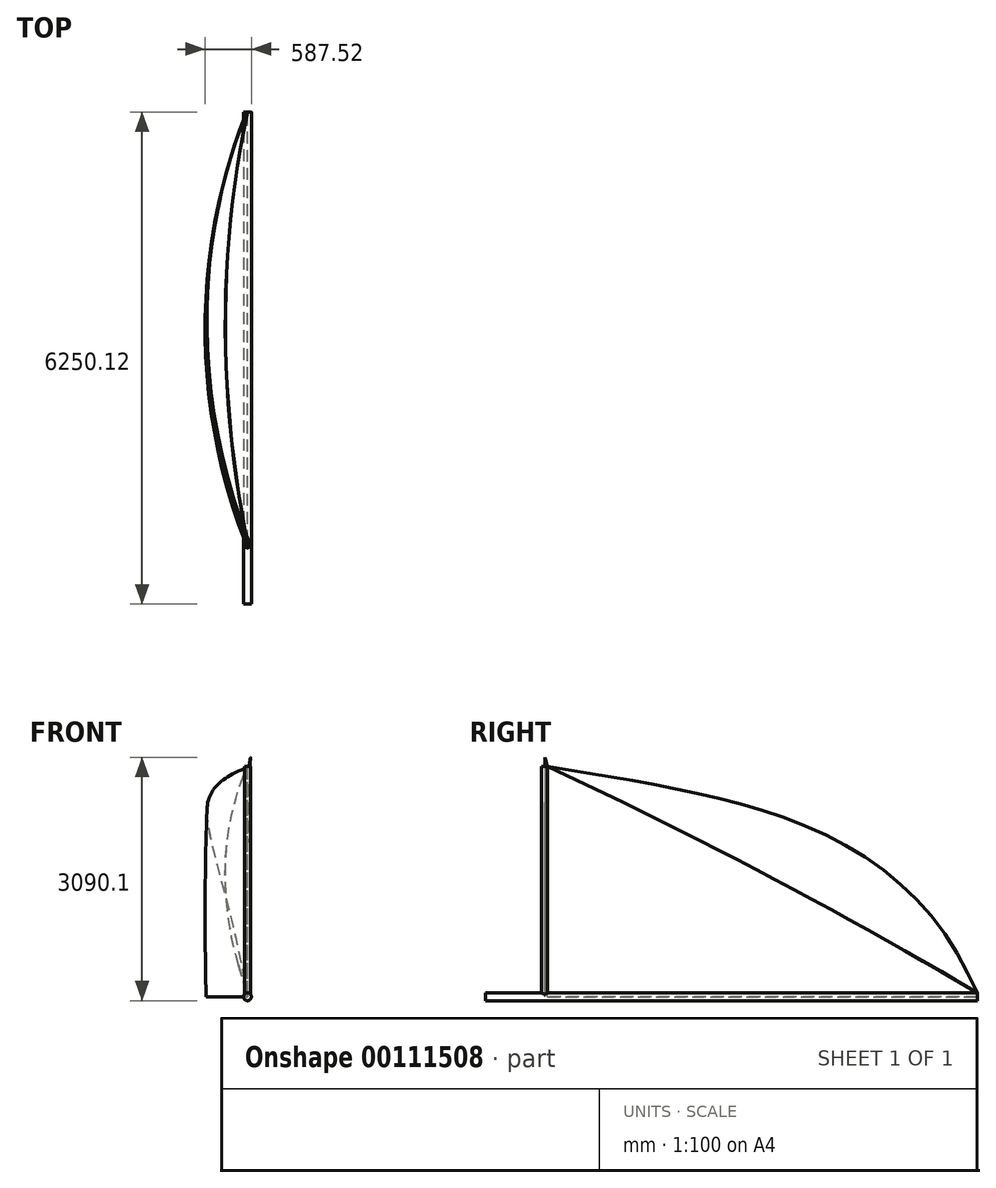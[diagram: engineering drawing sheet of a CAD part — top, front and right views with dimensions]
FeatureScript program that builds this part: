
annotation { "Feature Type Name" : "Feature", "Feature Type Description" : "" }
export const myFeature = defineFeature(function(context is Context, id is Id, definition is map)
    precondition{}
    {
        {
            var Q0;
            Q0=qCreatedBy(makeId("Front.planeOp"),FACE);
            var sketch = newSketch(context, id + "F0", { "sketchPlane" : qUnion([Q0])});
            skCircle(sketch, "E0", {"center": v(0, 0) * mm, "radius": 50 * mm});
            skSolve(sketch);
        }
        {
            var Q0;
            Q0=qSketchRegion(id+"F0",true);
            extrude(context, id + "F1", {"entities" : qUnion([Q0]), "oppositeDirection" : true, "depth" : 6250 * mm});
        }
        {
            var Q0;
            Q0=qCreatedBy(makeId("Top.planeOp"),FACE);
            var sketch = newSketch(context, id + "F2", { "sketchPlane" : qUnion([Q0])});
            skLineSegment(sketch, "E1", {"start": v(-50, 0) * mm, "end": v(-50, 6250) * mm});
            skLineSegment(sketch, "E2", {"start": v(50, 6250) * mm, "end": v(50, 0) * mm});
            skLineSegment(sketch, "E3", {"start": v(0, 750) * mm, "end": v(-50, 750) * mm});
            skLineSegment(sketch, "E4", {"start": v(0, 750) * mm, "end": v(50, 750) * mm});
            skCircle(sketch, "E5", {"center": v(0, 750) * mm, "radius": 37.5 * mm});
            skSolve(sketch);
        }
        {
            var Q0;
            Q0=qSketchRegion(id+"F2",true);
            extrude(context, id + "F3", {"entities" : qUnion([Q0]), "operationType" : NewBodyOperationType.ADD, "depth" : 2925 * mm});
        }
        {
            var Q0;
            Q0=qCreatedBy(makeId("Top.planeOp"),FACE);
            var sketch = newSketch(context, id + "F4", { "sketchPlane" : qUnion([Q0])});
            skPoint(sketch, "E6.0", {"position": v(0, 750) * mm});
            skLineSegment(sketch, "E7.0", {"start": v(50, 6250) * mm, "end": v(-50, 6250) * mm});
            skPoint(sketch, "E8", {"position": v(0, 6250) * mm});
            skArc(sketch, "E9", {"start": v(0, 6250) * mm, "mid": v(-524.4, 3500) * mm, "end": v(0, 750) * mm});
            skLineSegment(sketch, "E10", {"start": v(6948.32, -1070.1) * mm, "end": v(6948.32, 10785.69) * mm, "construction": true});
            skArc(sketch, "E11.0", {"start": v(-1.08, 6250) * mm, "mid": v(-525.4, 3500) * mm, "end": v(-1.08, 750) * mm});
            skLineSegment(sketch, "E12", {"start": v(0, 6250) * mm, "end": v(-1.08, 6250) * mm});
            skLineSegment(sketch, "E13", {"start": v(0, 750) * mm, "end": v(-1.08, 750) * mm});
            skSolve(sketch);
        }
        {
            var Q0;
            Q0=qSketchRegion(id+"F4",true);
            var Q1;
            Q1=sQuery(id+"F4.wireOp",EDGE,"E9");
            var Q2;
            Q2=sQuery(id+"F4.wireOp",EDGE,"E10");
            revolve(context, id + "F5", {"bodyType" : ToolBodyType.SURFACE, "entities" : qUnion([Q0]), "surfaceEntities" : qUnion([Q1]), "axis" : qUnion([Q2]), "revolveType" : RevolveType.FULL});
        }
        {
            var Q0;
            Q0=qCreatedBy(makeId("Top.planeOp"),FACE);
            cPlane(context, id + "F6", {"entities" : qUnion([Q0]), "cplaneType" : CPlaneType.OFFSET, "offset" : 1000 * mm, "width" : 150 * mm, "height" : 150 * mm});
        }
        {
            var Q0;
            Q0=qCreatedBy(id+"F6.planeOp",FACE);
            var sketch = newSketch(context, id + "F7", { "sketchPlane" : qUnion([Q0])});
            skLineSegment(sketch, "E14", {"start": v(41794.72, -2246.79) * mm, "end": v(45677.07, -23348.96) * mm, "construction": true});
            skSolve(sketch);
        }
        {
            var Q0;
            Q0=makeQuery(id+"F4.imprint","IMPRINT",FACE,{"disambiguationData":[TD([[makeQuery(id+"F4.imprint","IMPRINT",EDGE,{"derivedFrom":sQuery(id+"F4.wireOp",EDGE,"E9")}),-1.0]])]});
            var Q1;
            Q1=sQuery(id+"F4.wireOp",EDGE,"E9");
            var Q2;
            Q2=sQuery(id+"F7.wireOp",EDGE,"E14");
            revolve(context, id + "F8", {"entities" : qUnion([Q0]), "surfaceEntities" : qUnion([Q1]), "axis" : qUnion([Q2]), "revolveType" : RevolveType.ONE_DIRECTION, "oppositeDirection" : true, "angle" : 12 * degree});
        }
        {
            var Q0;
            Q0=qCreatedBy(makeId("Right.planeOp"),FACE);
            var sketch = newSketch(context, id + "F9", { "sketchPlane" : qUnion([Q0])});
            skLineSegment(sketch, "E15.0", {"start": v(712.5, 2925) * mm, "end": v(787.5, 2925) * mm});
            skLineSegment(sketch, "E16.0", {"start": v(6250, -50) * mm, "end": v(6250, 50) * mm});
            skFitSpline(sketch, "E17", {"points": [v(6250, 50) * mm, v(5690.7, 991.83) * mm, v(4190.9, 2116.67) * mm, v(787.5, 2925) * mm], "startDerivative": vector(-1887.64, 3853.18) * mm, "endDerivative": vector(-8543.52, 1369.23) * mm});
            skLineSegment(sketch, "E18", {"start": v(6250, 50) * mm, "end": v(32368.7, 50) * mm});
            skLineSegment(sketch, "E19", {"start": v(32368.7, 50) * mm, "end": v(29612.32, 45971.36) * mm});
            skLineSegment(sketch, "E20", {"start": v(29612.32, 45971.36) * mm, "end": v(-10598.41, 45971.36) * mm});
            skLineSegment(sketch, "E21", {"start": v(-10598.41, 45971.36) * mm, "end": v(787.5, 2925) * mm});
            skSolve(sketch);
        }
        {
            var Q0;
            Q0=makeQuery(id+"F9.imprint","IMPRINT",FACE,{"disambiguationData":[TD([[makeQuery(id+"F9.imprint","IMPRINT",EDGE,{"derivedFrom":sQuery(id+"F9.wireOp",EDGE,"E17")}),-1.0]])]});
            extrude(context, id + "F10", {"entities" : qUnion([Q0]), "operationType" : NewBodyOperationType.REMOVE, "endBound" : BoundingType.SYMMETRIC, "depth" : 9330.88 * mm});
        }
        {
            var Q0;
            Q0=qCreatedBy(makeId("Right.planeOp"),FACE);
            var sketch = newSketch(context, id + "F11", { "sketchPlane" : qUnion([Q0])});
            skLineSegment(sketch, "E22.0", {"start": v(712.5, 2925) * mm, "end": v(787.5, 2925) * mm});
            skPoint(sketch, "E22.1", {"position": v(6250, 0) * mm});
            skPoint(sketch, "E23", {"position": v(750, 2925) * mm});
            skLineSegment(sketch, "E24.0", {"start": v(6250, -50) * mm, "end": v(6250, 50) * mm});
            skLineSegment(sketch, "E25", {"start": v(6250, 50) * mm, "end": v(787.5, 2925) * mm, "construction": true});
            skSolve(sketch);
        }
        {
            var Q0;
            Q0=sQuery(id+"F11.wireOp",EDGE,"E25");
            cPlane(context, id + "F12", {"entities" : qUnion([Q0]), "cplaneType" : CPlaneType.LINE_ANGLE, "offset" : 150 * mm, "angle" : 165 * degree, "width" : 150 * mm, "height" : 150 * mm});
        }
        {
            var Q0;
            Q0=qCreatedBy(id+"F12.planeOp",FACE);
            var sketch = newSketch(context, id + "F13", { "sketchPlane" : qUnion([Q0])});
            skLineSegment(sketch, "E26.0", {"start": v(-764.85, 5507.45) * mm, "end": v(-764.85, -665.44) * mm, "construction": true});
            skArc(sketch, "E27", {"start": v(-764.85, 5507.45) * mm, "mid": v(-1055.2, 2421) * mm, "end": v(-764.85, -665.44) * mm});
            skArc(sketch, "E28.0", {"start": v(-765.87, 5507.45) * mm, "mid": v(-1056.2, 2421) * mm, "end": v(-765.87, -665.44) * mm});
            skLineSegment(sketch, "E29", {"start": v(-764.85, 5507.45) * mm, "end": v(-765.87, 5507.45) * mm});
            skLineSegment(sketch, "E30", {"start": v(-764.85, -665.44) * mm, "end": v(-765.87, -665.44) * mm});
            skSolve(sketch);
        }
        {
            var Q0;
            Q0=qCreatedBy(makeId("Top.planeOp"),FACE);
            var sketch = newSketch(context, id + "F14", { "sketchPlane" : qUnion([Q0])});
            skLineSegment(sketch, "E31.0", {"start": v(50, 6250) * mm, "end": v(-50, 6250) * mm});
            skPoint(sketch, "E32.0", {"position": v(0, 787.5) * mm});
            skLineSegment(sketch, "E33.bottom", {"start": v(0, 787.5) * mm, "end": v(-1, 787.5) * mm});
            skLineSegment(sketch, "E33.top", {"start": v(0, 6250) * mm, "end": v(-1, 6250) * mm});
            skLineSegment(sketch, "E33.left", {"start": v(0, 787.5) * mm, "end": v(0, 6250) * mm});
            skLineSegment(sketch, "E33.right", {"start": v(-1, 787.5) * mm, "end": v(-1, 6250) * mm});
            skSolve(sketch);
        }
        {
            var Q0;
            Q0=makeQuery(id+"F14.imprint","IMPRINT",FACE,{"disambiguationData":[TD([[makeQuery(id+"F14.imprint","IMPRINT",EDGE,{"derivedFrom":sQuery(id+"F14.wireOp",EDGE,"E33.bottom")}),-1.0]])]});
            var Q1;
            Q1=makeQuery(id+"F13.imprint","IMPRINT",FACE,{"disambiguationData":[TD([[makeQuery(id+"F13.imprint","IMPRINT",EDGE,{"derivedFrom":sQuery(id+"F13.wireOp",EDGE,"E27")}),-1.0]])]});
            loft(context, id + "F15", {"sheetProfilesArray" : [{ "sheetProfileEntities" : qUnion([Q0]) }, { "sheetProfileEntities" : qUnion([Q1]) }]});
        }
    });
